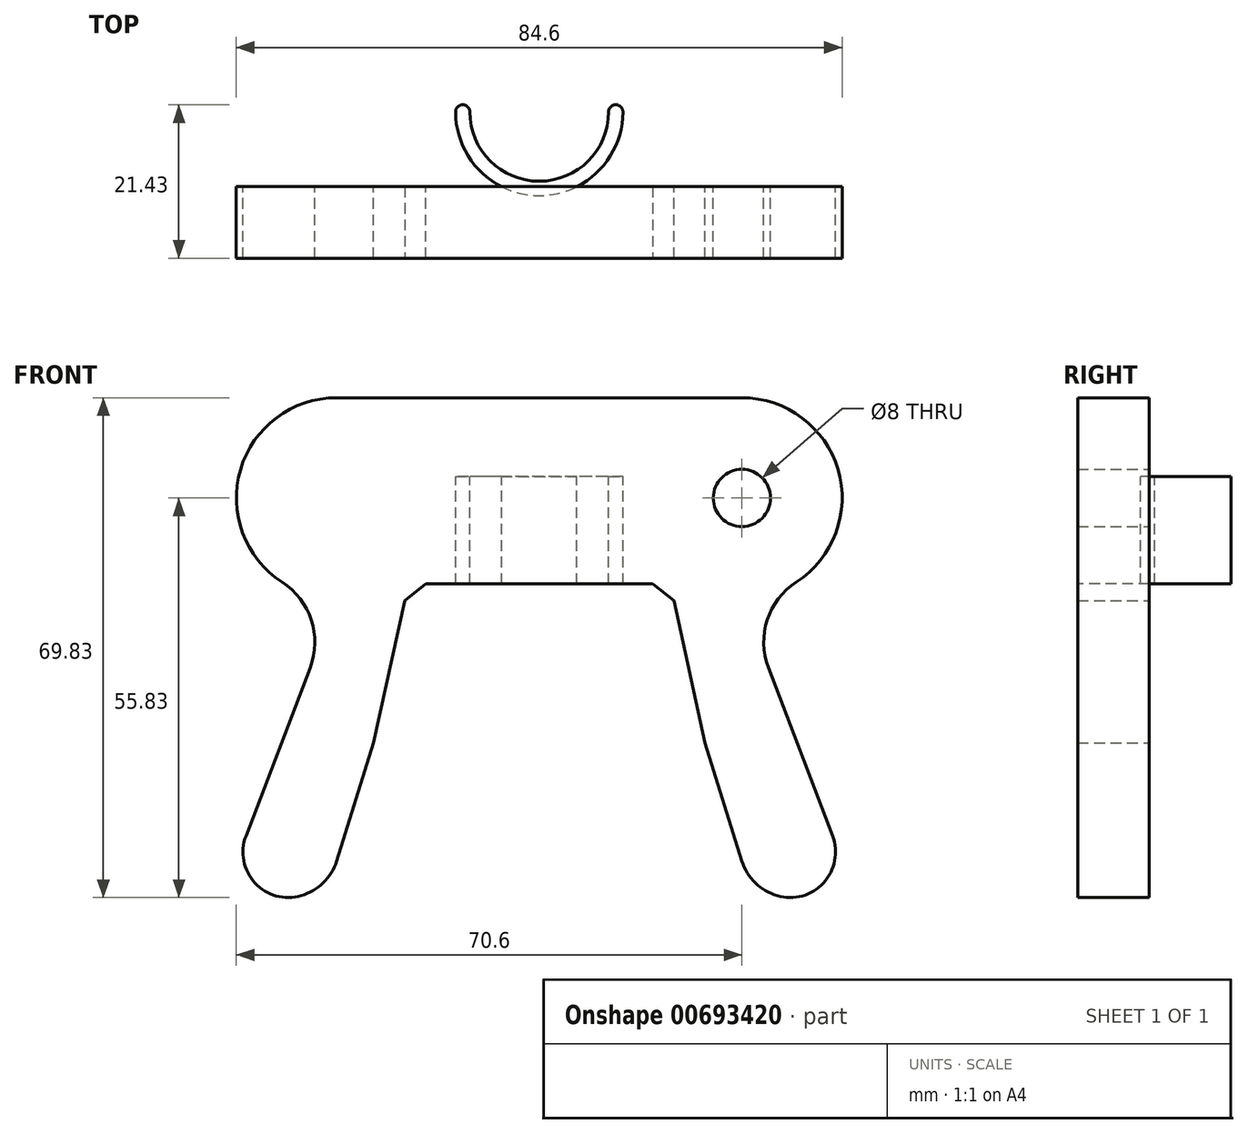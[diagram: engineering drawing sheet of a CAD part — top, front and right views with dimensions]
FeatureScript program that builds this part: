
annotation { "Feature Type Name" : "Feature", "Feature Type Description" : "" }
export const myFeature = defineFeature(function(context is Context, id is Id, definition is map)
    precondition{}
    {
        {
            var Q0;
            Q0=qCreatedBy(makeId("Front.planeOp"),FACE);
            var sketch = newSketch(context, id + "F0", { "sketchPlane" : qUnion([Q0])});
            skCircle(sketch, "E0", {"center": v(-28.3, 0) * mm, "radius": 4 * mm});
            skLineSegment(sketch, "E1", {"start": v(0, 34.2) * mm, "end": v(0, -32.83) * mm, "construction": true});
            skArc(sketch, "E2", {"start": v(-35.9, -11.75) * mm, "mid": v(-41.73, 3.97) * mm, "end": v(-28.3, 14) * mm});
            skLineSegment(sketch, "E3", {"start": v(-28.3, 14) * mm, "end": v(0, 14) * mm});
            skLineSegment(sketch, "E4", {"start": v(-28.3, -14) * mm, "end": v(0, -14) * mm, "construction": true});
            skLineSegment(sketch, "E5", {"start": v(-32, -23.7) * mm, "end": v(-40.96, -47.22) * mm});
            skLineSegment(sketch, "E6", {"start": v(-42.28, -0.72) * mm, "end": v(-42.3, -76.48) * mm, "construction": true});
            skPoint(sketch, "E6.endSnap0", {"position": v(-42.3, 0) * mm});
            skArc(sketch, "E7", {"start": v(-33.26, -55.58) * mm, "mid": v(-30.17, -53.77) * mm, "end": v(-28.3, -50.72) * mm});
            skLineSegment(sketch, "E8", {"start": v(-28.3, -50.72) * mm, "end": v(-23.13, -34.19) * mm});
            skPoint(sketch, "E9.orphan", {"position": v(-16.82, -14) * mm});
            skPoint(sketch, "E10.visualSharp", {"position": v(-42.3, -50.72) * mm});
            skArc(sketch, "E10.filletArc", {"start": v(-40.96, -47.22) * mm, "mid": v(-39.7, -53.78) * mm, "end": v(-33.26, -55.58) * mm});
            skPoint(sketch, "E11.visualSharp", {"position": v(-22.56, -32.36) * mm});
            skPoint(sketch, "E12.visualSharp", {"position": v(-28.3, -14) * mm});
            skArc(sketch, "E12.filletArc", {"start": v(-32, -23.7) * mm, "mid": v(-31.84, -17.04) * mm, "end": v(-35.9, -11.75) * mm});
            skPoint(sketch, "E13.MirrorP", {"position": v(22.56, -32.36) * mm});
            skLineSegment(sketch, "E14.MirrorCS", {"start": v(28.3, -50.72) * mm, "end": v(23.13, -34.19) * mm});
            skArc(sketch, "E15.MirrorCS", {"start": v(33.26, -55.58) * mm, "mid": v(30.17, -53.77) * mm, "end": v(28.3, -50.72) * mm});
            skArc(sketch, "E16.MirrorCS", {"start": v(40.96, -47.22) * mm, "mid": v(39.7, -53.78) * mm, "end": v(33.26, -55.58) * mm});
            skLineSegment(sketch, "E17.MirrorCS", {"start": v(32, -23.7) * mm, "end": v(40.96, -47.22) * mm});
            skArc(sketch, "E18.MirrorCS", {"start": v(32, -23.7) * mm, "mid": v(31.84, -17.04) * mm, "end": v(35.9, -11.75) * mm});
            skCircle(sketch, "E19.MirrorC", {"center": v(28.3, 0) * mm, "radius": 4 * mm});
            skArc(sketch, "E20.MirrorCS", {"start": v(35.9, -11.75) * mm, "mid": v(41.73, 3.97) * mm, "end": v(28.3, 14) * mm});
            skLineSegment(sketch, "E21.MirrorCS", {"start": v(28.3, 14) * mm, "end": v(0, 14) * mm});
            skPoint(sketch, "E22.visualSharp", {"position": v(0, -14) * mm});
            skLineSegment(sketch, "E23", {"start": v(-15, 3) * mm, "end": v(15, 3) * mm});
            skPoint(sketch, "E24.MirrorCS.end.orphan", {"position": v(23.13, -34.19) * mm});
            skPoint(sketch, "E24.MirrorCS.start.orphan", {"position": v(21.08, -31.15) * mm});
            skPoint(sketch, "E25.start.orphan", {"position": v(-21.08, -31.15) * mm});
            skLineSegment(sketch, "E26", {"start": v(-15, 3) * mm, "end": v(-23.13, -34.19) * mm});
            skLineSegment(sketch, "E27", {"start": v(15, 3) * mm, "end": v(23.13, -34.19) * mm});
            skLineSegment(sketch, "E28", {"start": v(-28.3, 0) * mm, "end": v(28.3, 0) * mm, "construction": true});
            skSolve(sketch);
        }
        {
            var Q0;
            Q0=makeQuery(id+"F0.imprint","IMPRINT",FACE,{"disambiguationData":[TD([[makeQuery(id+"F0.imprint","IMPRINT",EDGE,{"derivedFrom":sQuery(id+"F0.wireOp",EDGE,"E0")}),-1.0]])]});
            var Q1;
            Q1=makeQuery(id+"F0.imprint","IMPRINT",FACE,{"disambiguationData":[TD([[makeQuery(id+"F0.imprint","IMPRINT",EDGE,{"derivedFrom":sQuery(id+"F0.wireOp",EDGE,"E19.MirrorC")}),-1.0]])]});
            var Q2;
            Q2=makeQuery(id+"F0.imprint","IMPRINT",FACE,{"disambiguationData":[TD([[makeQuery(id+"F0.imprint","IMPRINT",EDGE,{"derivedFrom":sQuery(id+"F0.wireOp",EDGE,"E0")}),1.0]])]});
            extrude(context, id + "F1", {"entities" : qUnion([Q0, Q1, Q2]), "depth" : 35 * mm, "offsetDistance" : 25 * mm});
        }
        {
            var Q0;
            Q0=makeQuery(id+"F0.imprint","IMPRINT",FACE,{"disambiguationData":[TD([[makeQuery(id+"F0.imprint","IMPRINT",EDGE,{"derivedFrom":sQuery(id+"F0.wireOp",EDGE,"E19.MirrorC")}),-1.0]])]});
            var Q1;
            Q1=makeQuery(id+"F0.imprint","IMPRINT",FACE,{"disambiguationData":[TD([[makeQuery(id+"F0.imprint","IMPRINT",EDGE,{"derivedFrom":sQuery(id+"F0.wireOp",EDGE,"E0")}),1.0]])]});
            extrude(context, id + "F2", {"entities" : qUnion([Q0, Q1]), "operationType" : NewBodyOperationType.REMOVE, "depth" : 25 * mm, "offsetDistance" : 25 * mm});
        }
        {
            var Q0;
            Q0=makeQuery(id+"F1.opExtrude","SWEPT_FACE",FACE,{"disambiguationData":[OSD([sQuery(id+"F0.wireOp",EDGE,"E23")])]});
            var sketch = newSketch(context, id + "F3", { "sketchPlane" : qUnion([Q0])});
            skCircle(sketch, "E29", {"center": v(0, 14.57) * mm, "radius": 7 * mm});
            skPoint(sketch, "E29.centerSnap0", {"position": v(0, 35) * mm});
            skArc(sketch, "E30", {"start": v(-11.68, 14.57) * mm, "mid": v(0, 26.25) * mm, "end": v(11.68, 14.57) * mm});
            skArc(sketch, "E31.0", {"start": v(-9.68, 14.57) * mm, "mid": v(0, 24.25) * mm, "end": v(9.68, 14.57) * mm});
            skArc(sketch, "E32", {"start": v(-11.68, 14.57) * mm, "mid": v(-10.68, 13.57) * mm, "end": v(-9.68, 14.57) * mm});
            skArc(sketch, "E33", {"start": v(9.68, 14.57) * mm, "mid": v(10.68, 13.57) * mm, "end": v(11.68, 14.57) * mm});
            skLineSegment(sketch, "E34", {"start": v(-10.68, 13.57) * mm, "end": v(-15, 13.57) * mm});
            skLineSegment(sketch, "E35", {"start": v(10.68, 13.57) * mm, "end": v(15, 13.57) * mm});
            skCircle(sketch, "E36", {"center": v(0, 14.57) * mm, "radius": 8.25 * mm});
            skSolve(sketch);
        }
        {
            var Q0;
            Q0=makeQuery(id+"F3.imprint","IMPRINT",FACE,{"disambiguationData":[TD([[makeQuery(id+"F3.imprint","IMPRINT",EDGE,{"derivedFrom":sQuery(id+"F3.wireOp",EDGE,"E29")}),1.0]])]});
            extrude(context, id + "F4", {"entities" : qUnion([Q0]), "operationType" : NewBodyOperationType.REMOVE, "oppositeDirection" : true, "depth" : 25 * mm, "offsetDistance" : 25 * mm});
        }
        {
            var Q0;
            Q0=makeQuery(id+"F3.imprint","IMPRINT",FACE,{"disambiguationData":[TD([[makeQuery(id+"F3.imprint","IMPRINT",EDGE,{"derivedFrom":sQuery(id+"F3.wireOp",EDGE,"E30")}),-1.0]])]});
            var Q1;
            {var subQ2=sQuery(id+"F3.wireOp",EDGE,"E30");Q1=makeQuery(id+"F3.imprint","IMPRINT",FACE,{"disambiguationData":[TD([[makeQuery(id+"F3.imprint","IMPRINT",EDGE,{"derivedFrom":subQ2}),1.0]])]});}
            extrude(context, id + "F5", {"entities" : qUnion([Q0, Q1]), "operationType" : NewBodyOperationType.ADD, "depth" : 15 * mm, "offsetDistance" : 25 * mm});
        }
        {
            var Q0;
            Q0=makeQuery(id+"F5.opExtrude","SWEPT_FACE",FACE,{"disambiguationData":[OSD([sQuery(id+"F0.wireOp",EDGE,"E23"),sQuery(id+"F0.wireOp",EDGE,"E26")])]});
            extrude(context, id + "F6", {"entities" : qUnion([Q0]), "operationType" : NewBodyOperationType.ADD, "depth" : 5 * mm, "offsetDistance" : 25 * mm});
        }
        {
            var Q0;
            Q0=makeQuery(id+"F5.opExtrude","SWEPT_FACE",FACE,{"disambiguationData":[OSD([sQuery(id+"F0.wireOp",EDGE,"E23"),sQuery(id+"F0.wireOp",EDGE,"E27")])]});
            extrude(context, id + "F7", {"entities" : qUnion([Q0]), "operationType" : NewBodyOperationType.ADD, "depth" : 5 * mm, "offsetDistance" : 25 * mm});
        }
        {
            var Q0;
            {var subQ0=sQuery(id+"F0.wireOp",EDGE,"E26");var subQ1=sQuery(id+"F0.wireOp",EDGE,"E23");Q0=makeQuery(id+"F6.boolean.opBoolean","INTERSECT",EDGE,{"derivedFrom":[makeQuery(id+"F1.opExtrude","SWEPT_FACE",FACE,{"disambiguationData":[OSD([subQ0])]}),makeQuery(id+"F6.opExtrude","SWEPT_FACE",FACE,{"disambiguationData":[OSD([subQ1,subQ0]),TDD([makeQuery(id+"F5.opExtrude","CAP_EDGE",EDGE,{"disambiguationData":[OSD([subQ1,subQ0])],"isStart":false})])]})]});}
            var Q1;
            {var subQ0=sQuery(id+"F0.wireOp",EDGE,"E27");var subQ1=sQuery(id+"F0.wireOp",EDGE,"E23");Q1=makeQuery(id+"F7.boolean.opBoolean","INTERSECT",EDGE,{"derivedFrom":[makeQuery(id+"F1.opExtrude","SWEPT_FACE",FACE,{"disambiguationData":[OSD([subQ0])]}),makeQuery(id+"F7.opExtrude","SWEPT_FACE",FACE,{"disambiguationData":[OSD([subQ1,subQ0]),TDD([makeQuery(id+"F5.opExtrude","CAP_EDGE",EDGE,{"disambiguationData":[OSD([subQ1,subQ0])],"isStart":false})])]})]});}
            var Q2;
            Q2=makeQuery(id+"F5.opExtrude","CAP_EDGE",EDGE,{"disambiguationData":[OSD([sQuery(id+"F3.wireOp",EDGE,"E31.0")])],"isStart":true});
            var Q3;
            Q3=makeQuery(id+"F5.boolean.opBoolean","SPLIT",EDGE,{"derivedFrom":makeQuery(id+"F1.opExtrude","SWEPT_EDGE",EDGE,{"disambiguationData":[OSD([sQuery(id+"F0.wireOp",EDGE,"E23"),sQuery(id+"F0.wireOp",EDGE,"E26")])]})});
            var Q4;
            Q4=makeQuery(id+"F5.boolean.opBoolean","SPLIT",EDGE,{"derivedFrom":makeQuery(id+"F1.opExtrude","SWEPT_EDGE",EDGE,{"disambiguationData":[OSD([sQuery(id+"F0.wireOp",EDGE,"E23"),sQuery(id+"F0.wireOp",EDGE,"E27")])]})});
            chamfer(context, id + "F8", {"entities" : qUnion([Q0, Q1, Q2, Q3, Q4]), "width" : 3 * mm, "tangentPropagation" : true});
        }
        {
            var Q0;
            Q0=makeQuery(id+"F3.imprint","IMPRINT",FACE,{"disambiguationData":[TD([[makeQuery(id+"F3.imprint","IMPRINT",EDGE,{"derivedFrom":sQuery(id+"F3.wireOp",EDGE,"E29")}),-1.0]])]});
            extrude(context, id + "F9", {"entities" : qUnion([Q0]), "operationType" : NewBodyOperationType.REMOVE, "endBound" : BoundingType.SYMMETRIC, "oppositeDirection" : true, "depth" : 10 * mm, "offsetDistance" : 25 * mm});
        }
        {
            var Q0;
            Q0=makeQuery(id+"F1.opExtrude","SWEPT_FACE",FACE,{"disambiguationData":[OSD([sQuery(id+"F0.wireOp",EDGE,"E3"),sQuery(id+"F0.wireOp",EDGE,"E21.MirrorCS")])]});
            var sketch = newSketch(context, id + "F10", { "sketchPlane" : qUnion([Q0])});
            skCircle(sketch, "E37", {"center": v(0, -14.57) * mm, "radius": 8.25 * mm});
            skSolve(sketch);
        }
        {
            var Q0;
            Q0=makeQuery(id+"F10.imprint","IMPRINT",FACE,{"disambiguationData":[TD([[makeQuery(id+"F10.imprint","IMPRINT",EDGE,{"derivedFrom":sQuery(id+"F10.wireOp",EDGE,"E37")}),1.0]])]});
            extrude(context, id + "F11", {"entities" : qUnion([Q0]), "operationType" : NewBodyOperationType.REMOVE, "oppositeDirection" : true, "depth" : 5 * mm, "offsetDistance" : 25 * mm});
        }
    });
